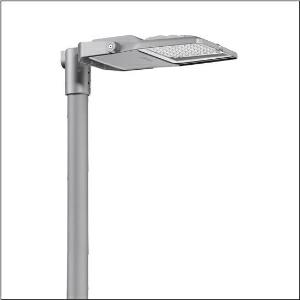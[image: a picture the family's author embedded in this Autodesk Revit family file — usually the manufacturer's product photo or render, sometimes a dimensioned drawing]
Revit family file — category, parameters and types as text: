
# Revit family: floodlight_fl_21_iq_mini___pl33t_5xa7771b2f3a_2789
name_source: partatom
category: Lighting Fixtures
units: mm (PartAtom-declared; Revit-internal decimal feet)

## family parameters
Cut with Voids When Loaded = No
Host = Face
Light Source = No
Part Type = Normal
Room Calculation Point = No
Round Connector Dimension = Use Diameter
Shared = No

## types (1)
- --- (1 x LED, 6170 lm, 45.5 W, 3000K)
    Apparent Load = 46 VA
    CIE Flux Codes = 26 75 99 100 100
    Color Rendering = 70
    Color Temperature = 3000K
    Default Elevation = 1800 mm
    Description = Floodlight FL 21 iQ mini, floodlight, primary light control with lens, of PMMA, primary optical cover: protective disc, of toughened safety glass, transparent, light distribution: PL33T, light emission: direct distribution, installation type: surface-mounted, LED, High Power LED, rated luminous flux: 6.170lm, luminous efficacy: 136lm/W, light colour: 730, colour temperature: 3000K, control: Auto-Match, Temp-Guard, Lumen-Switch, Night-Set, Smart-Wire, Light-Fading, Desk-Remote (wireless, voltage-free reading and setting of iQ features in the workshop via application-optimized NFC function/RFID function), optimised constant luminous flux control (CLO 2.0), with terminal, 6-pole, mains connection: 220..240V, AC, 50/60Hz, start of lifetime: 46W, end of service life: 48W, reduction: 22W, luminaire housing, of diecast aluminium, powder-coated, Siteco® metallic grey (DB 702S), corrosivity category C5 mid according to DIN EN ISO 12944, sealing non-destructively replaceable, please order mast flange separately, mast bracket, of steel, galvanised, powder-coated, Siteco® metallic grey (DB 702S), protection rating (complete): IP66, insulation class (complete): insulation class II (safety insulation), certification: CE, ENEC, VDE, protection symbol: D, impact resistance: IK08, permissible operating ambient temperature: -40..+40°C, permissible operating ambient temperature for outdoor applications: -40..+50°C, standard: DIN EN 12944, LABS conformity tested according to VDMA 24364:2018-05, packaging unit: 1 piece

Light Distribution: PL33T
    Height = 70 mm
    Lamp = 1 x LED
    Lamp Light Flux = 6170 lm
    Lamp Power = 45.5 W
    Lamp count = 1
    Length = 485 mm
    Luminous efficacy = 136 lm/W
    Manufacturer = Siteco
    ModVariant = No
    Model = 5XA7771B2F3A
    Number of Poles = 1
    OnlyDefault = Yes
    Power Factor = 1
    Product Name = Floodlight FL 21 iQ mini | PL33T
    Product group = floodlight | pylon annexe
    ProductGroupID = 6200
    Protection Class = Protection class II
    Protection Degree = IP 66
    RLX_Detail_Level = 1
    RLX_Emergency_Light_Flux = 0 lm
    RLX_Emergency_Type = 0
    RLX_Emergency_Type_DB = No
    RlxData = <blob elided: 101173 chars, md5=a455143a>
    Socket = socket
    Standby Power = 0 W
    System Light Flux = 6170 lm
    System Power = 46 W
    Type Comments = factory setting: luminous flux: 100 % | dim-lin: 254 | 463 mA
    Type Image = l_1007125.jpg
    URL = http://relux.com
    VarID = @adj_082767
    Voltage = 0 V
    Weight = 0.00 kg
    Width = 337 mm

## geometry (parser evidence)
native form markers: Blend x4, Sweep x10
no freeform markers — native parametric forms only
